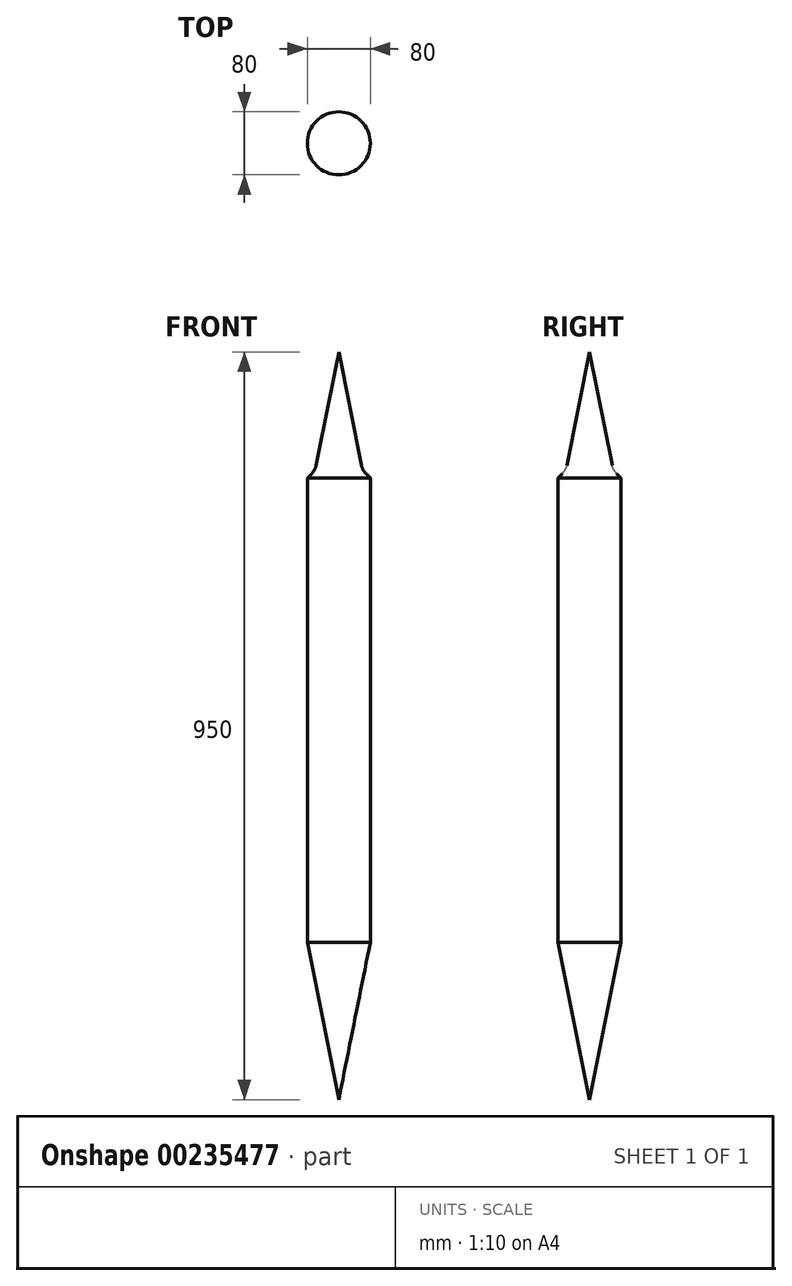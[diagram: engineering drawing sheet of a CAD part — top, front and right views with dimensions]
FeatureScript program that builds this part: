
annotation { "Feature Type Name" : "Feature", "Feature Type Description" : "" }
export const myFeature = defineFeature(function(context is Context, id is Id, definition is map)
    precondition{}
    {
        {
            var Q0;
            Q0=qCreatedBy(makeId("Front.planeOp"),FACE);
            var sketch = newSketch(context, id + "F0", { "sketchPlane" : qUnion([Q0])});
            skLineSegment(sketch, "E0.bottom", {"start": v(-30, 600) * mm, "end": v(30, 600) * mm});
            skLineSegment(sketch, "E0.top", {"start": v(-40, 0) * mm, "end": v(40, 0) * mm});
            skLineSegment(sketch, "E0.left", {"start": v(-40, 590) * mm, "end": v(-40, 0) * mm});
            skLineSegment(sketch, "E0.right", {"start": v(40, 590) * mm, "end": v(40, 0) * mm});
            skLineSegment(sketch, "E1", {"start": v(-40, 0) * mm, "end": v(0, -200) * mm});
            skLineSegment(sketch, "E2", {"start": v(0, -200) * mm, "end": v(40, 0) * mm});
            skLineSegment(sketch, "E3", {"start": v(-30, 600) * mm, "end": v(0, 750) * mm});
            skPoint(sketch, "E3.endSnap0", {"position": v(0, 600) * mm});
            skLineSegment(sketch, "E4", {"start": v(0, 750) * mm, "end": v(30, 600) * mm});
            skLineSegment(sketch, "E5", {"start": v(-30, 600) * mm, "end": v(-40, 590) * mm});
            skLineSegment(sketch, "E6.MirrorCS", {"start": v(30, 600) * mm, "end": v(40, 590) * mm});
            skPoint(sketch, "E7.MirrorCS.end.orphan", {"position": v(30, 600) * mm});
            skPoint(sketch, "E7.MirrorCS.start.orphan", {"position": v(40, 600) * mm});
            skPoint(sketch, "E8.orphan", {"position": v(-40, 600) * mm});
            skLineSegment(sketch, "E9", {"start": v(-30, 600) * mm, "end": v(-40, 600) * mm, "construction": true});
            skLineSegment(sketch, "E10", {"start": v(0, 750) * mm, "end": v(0, -200) * mm});
            skLineSegment(sketch, "E11", {"start": v(0, 930.53) * mm, "end": v(0, -394.73) * mm, "construction": true});
            skSolve(sketch);
        }
        {
            var Q0;
            {var subQ0=sQuery(id+"F0.wireOp",EDGE,"E3");Q0=makeQuery(id+"F0.imprint","IMPRINT",FACE,{"disambiguationData":[TD([[makeQuery(id+"F0.imprint","IMPRINT",EDGE,{"derivedFrom":subQ0}),-1.0]])]});}
            var Q1;
            {var subQ1=sQuery(id+"F0.wireOp",EDGE,"E0.left");Q1=makeQuery(id+"F0.imprint","IMPRINT",FACE,{"disambiguationData":[TD([[makeQuery(id+"F0.imprint","IMPRINT",EDGE,{"derivedFrom":subQ1}),1.0]])]});}
            var Q2;
            {var subQ0=sQuery(id+"F0.wireOp",EDGE,"E1");Q2=makeQuery(id+"F0.imprint","IMPRINT",FACE,{"disambiguationData":[TD([[makeQuery(id+"F0.imprint","IMPRINT",EDGE,{"derivedFrom":subQ0}),1.0]])]});}
            var Q3;
            Q3=sQuery(id+"F0.wireOp",EDGE,"E11");
            revolve(context, id + "F1", {"entities" : qUnion([Q0, Q1, Q2]), "axis" : qUnion([Q3]), "revolveType" : RevolveType.FULL});
        }
        {
            var Q0;
            Q0=makeQuery(id+"F1.opRevolve","SWEPT_EDGE",EDGE,{"disambiguationData":[OSD([sQuery(id+"F0.wireOp",EDGE,"E0.bottom"),sQuery(id+"F0.wireOp",EDGE,"E3"),sQuery(id+"F0.wireOp",EDGE,"E5")])]});
            fillet(context, id + "F2", {"entities" : qUnion([Q0]), "radius" : 20 * mm, "allowEdgeOverflow" : false});
        }
    });
